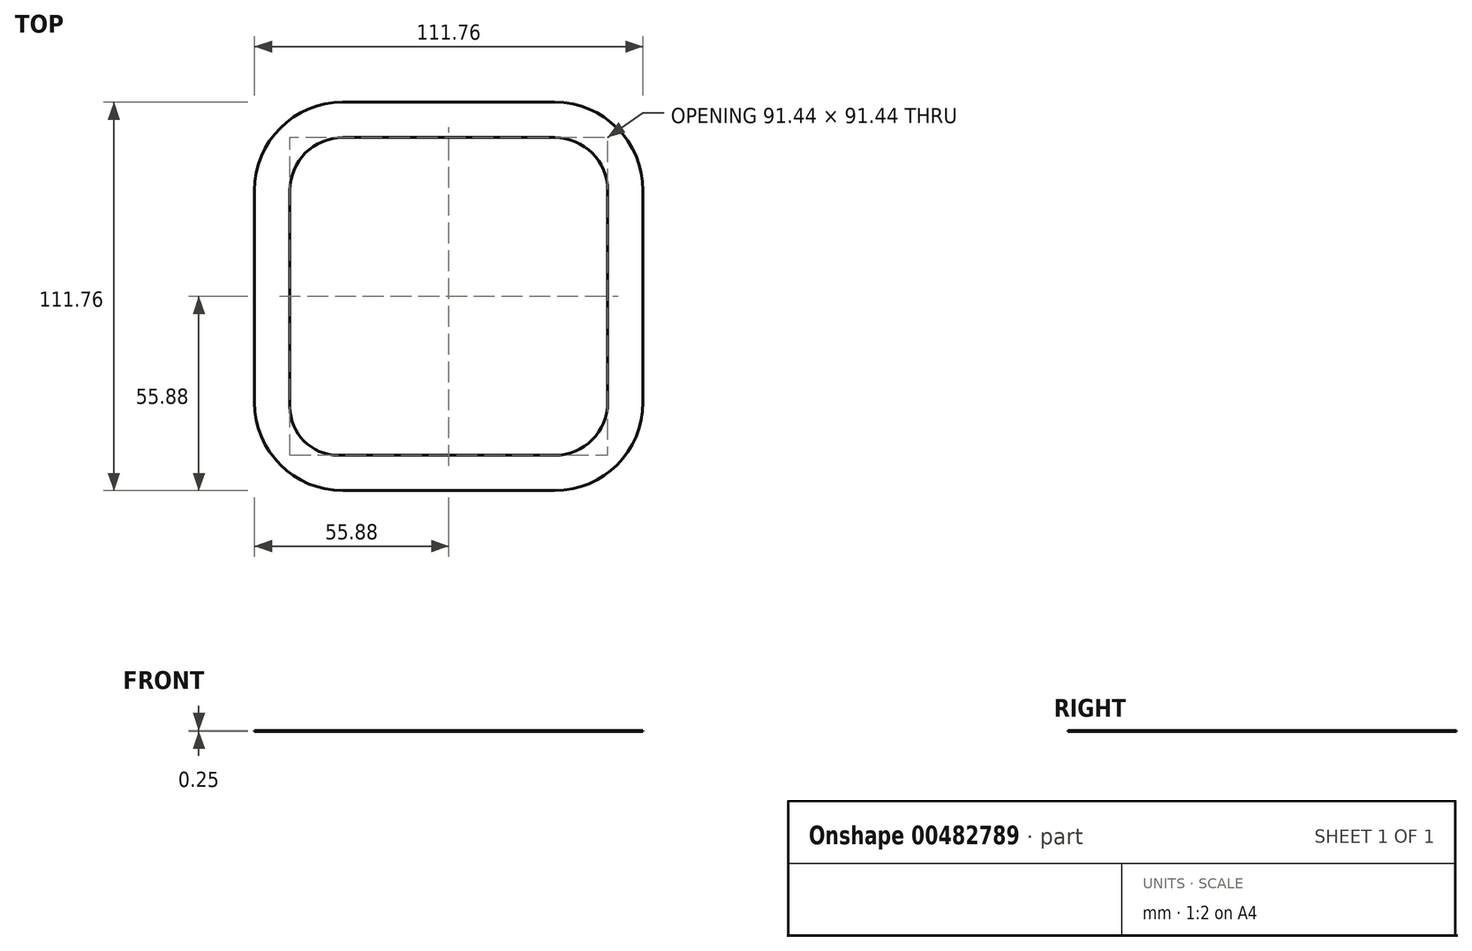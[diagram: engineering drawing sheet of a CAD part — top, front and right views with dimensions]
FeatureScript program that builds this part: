
annotation { "Feature Type Name" : "Feature", "Feature Type Description" : "" }
export const myFeature = defineFeature(function(context is Context, id is Id, definition is map)
    precondition{}
    {
        {
            var Q0;
            Q0=qCreatedBy(makeId("Top.planeOp"),FACE);
            var sketch = newSketch(context, id + "F0", { "sketchPlane" : qUnion([Q0])});
            skLineSegment(sketch, "E0.bottom", {"start": v(30.48, -45.72) * mm, "end": v(-31.75, -45.72) * mm});
            skLineSegment(sketch, "E0.top", {"start": v(30.48, 45.72) * mm, "end": v(-30.48, 45.72) * mm});
            skLineSegment(sketch, "E0.left", {"start": v(45.72, -30.48) * mm, "end": v(45.72, 30.48) * mm});
            skLineSegment(sketch, "E0.right", {"start": v(-45.72, -31.75) * mm, "end": v(-45.72, 30.48) * mm});
            skPoint(sketch, "E0.middle", {"position": v(0, 0) * mm});
            skPoint(sketch, "E1.visualSharp", {"position": v(-45.72, -45.72) * mm});
            skArc(sketch, "E1.filletArc", {"start": v(-45.72, -31.75) * mm, "mid": v(-41.63, -41.63) * mm, "end": v(-31.75, -45.72) * mm});
            skPoint(sketch, "E2.visualSharp", {"position": v(-45.72, 45.72) * mm});
            skArc(sketch, "E2.filletArc", {"start": v(-30.48, 45.72) * mm, "mid": v(-41.26, 41.26) * mm, "end": v(-45.72, 30.48) * mm});
            skPoint(sketch, "E3.visualSharp", {"position": v(45.72, 45.72) * mm});
            skArc(sketch, "E3.filletArc", {"start": v(45.72, 30.48) * mm, "mid": v(41.26, 41.26) * mm, "end": v(30.48, 45.72) * mm});
            skPoint(sketch, "E4.visualSharp", {"position": v(45.72, -45.72) * mm});
            skArc(sketch, "E4.filletArc", {"start": v(30.48, -45.72) * mm, "mid": v(41.26, -41.26) * mm, "end": v(45.72, -30.48) * mm});
            skLineSegment(sketch, "E5.bottom", {"start": v(30.48, -55.88) * mm, "end": v(-30.48, -55.88) * mm});
            skLineSegment(sketch, "E5.top", {"start": v(30.48, 55.88) * mm, "end": v(-30.48, 55.88) * mm});
            skLineSegment(sketch, "E5.left", {"start": v(55.88, -30.48) * mm, "end": v(55.88, 30.48) * mm});
            skLineSegment(sketch, "E5.right", {"start": v(-55.88, -30.48) * mm, "end": v(-55.88, 30.48) * mm});
            skPoint(sketch, "E6.visualSharp", {"position": v(-55.88, 55.88) * mm});
            skArc(sketch, "E6.filletArc", {"start": v(-30.48, 55.88) * mm, "mid": v(-48.44, 48.44) * mm, "end": v(-55.88, 30.48) * mm});
            skPoint(sketch, "E7.visualSharp", {"position": v(-55.88, -55.88) * mm});
            skArc(sketch, "E7.filletArc", {"start": v(-55.88, -30.48) * mm, "mid": v(-48.44, -48.44) * mm, "end": v(-30.48, -55.88) * mm});
            skPoint(sketch, "E8.visualSharp", {"position": v(55.88, -55.88) * mm});
            skArc(sketch, "E8.filletArc", {"start": v(30.48, -55.88) * mm, "mid": v(48.44, -48.44) * mm, "end": v(55.88, -30.48) * mm});
            skPoint(sketch, "E9.visualSharp", {"position": v(55.88, 55.88) * mm});
            skArc(sketch, "E9.filletArc", {"start": v(55.88, 30.48) * mm, "mid": v(48.44, 48.44) * mm, "end": v(30.48, 55.88) * mm});
            skSolve(sketch);
        }
        {
            var Q0;
            Q0 = qSketchRegion(id + "F0", true);
            extrude(context, id + "F1", {"entities" : qUnion([Q0]), "depth" : 0.25 * mm});
        }
    });
